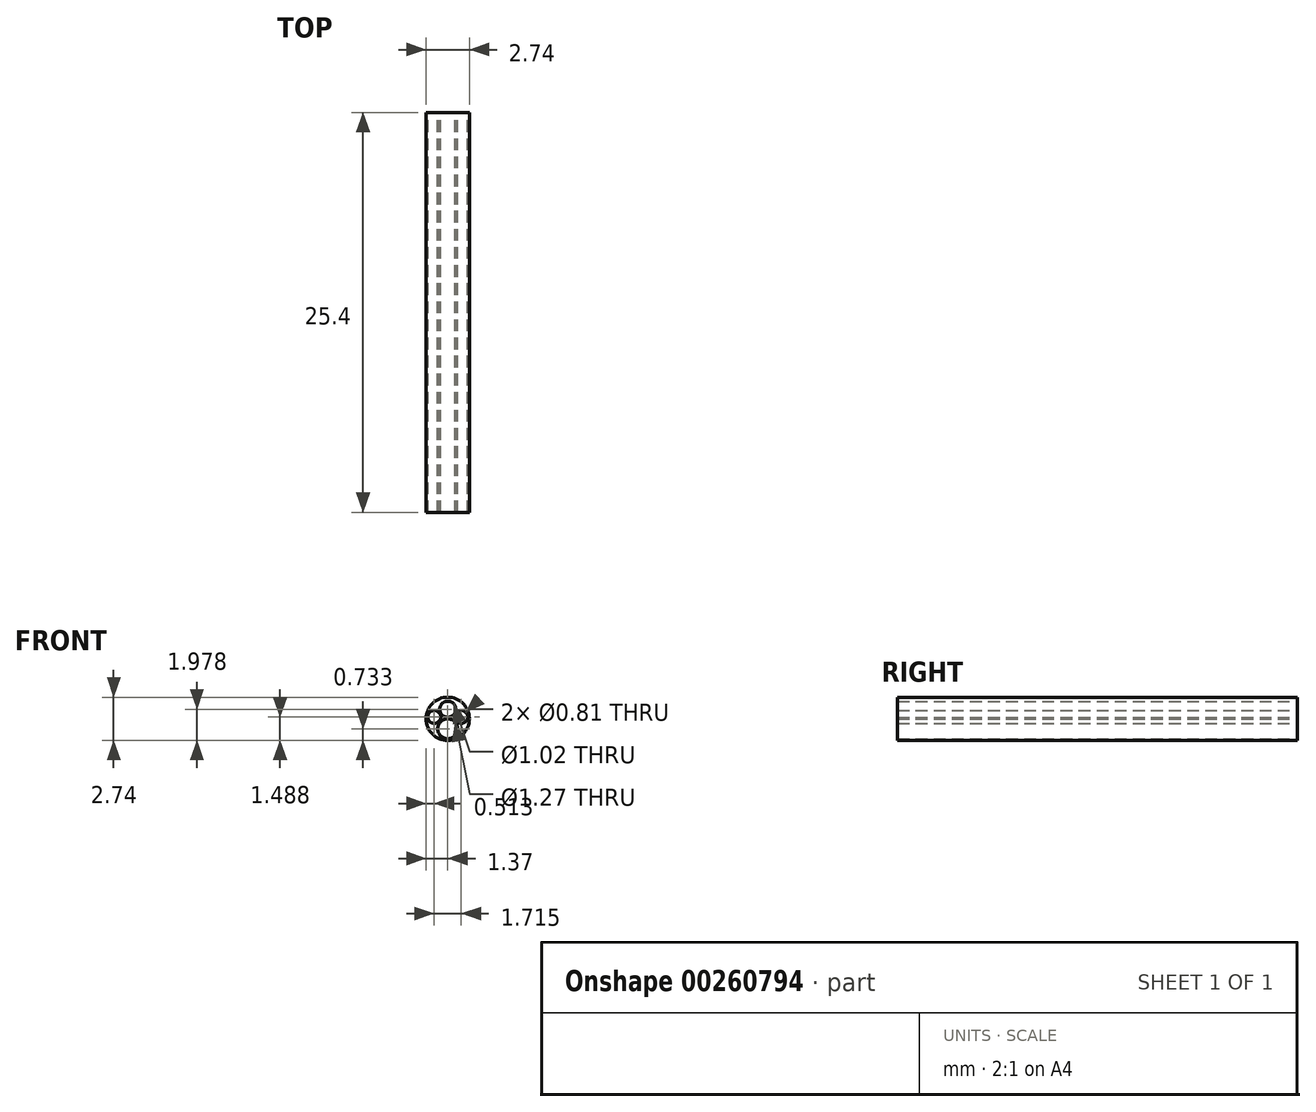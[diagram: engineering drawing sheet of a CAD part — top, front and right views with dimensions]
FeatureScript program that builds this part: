
annotation { "Feature Type Name" : "Feature", "Feature Type Description" : "" }
export const myFeature = defineFeature(function(context is Context, id is Id, definition is map)
    precondition{}
    {
        {
            var Q0;
            Q0=qCreatedBy(makeId("Front.planeOp"),FACE);
            var sketch = newSketch(context, id + "F0", { "sketchPlane" : qUnion([Q0])});
            skCircle(sketch, "E0", {"center": v(0, 0) * mm, "radius": 1.37 * mm});
            skCircle(sketch, "E1", {"center": v(0, 0.6) * mm, "radius": 0.5 * mm});
            skCircle(sketch, "E2", {"center": v(0, -0.64) * mm, "radius": 0.64 * mm});
            skCircle(sketch, "E3", {"center": v(0.86, 0.12) * mm, "radius": 0.4 * mm});
            skCircle(sketch, "E4", {"center": v(-0.86, 0.12) * mm, "radius": 0.4 * mm});
            skLineSegment(sketch, "E5", {"start": v(0, 1.37) * mm, "end": v(0, -1.37) * mm, "construction": true});
            skSolve(sketch);
        }
        {
            var Q0;
            Q0=qSketchRegion(id+"F0",true);
            extrude(context, id + "F1", {"entities" : qUnion([Q0]), "depth" : 25.4 * mm});
        }
    });
